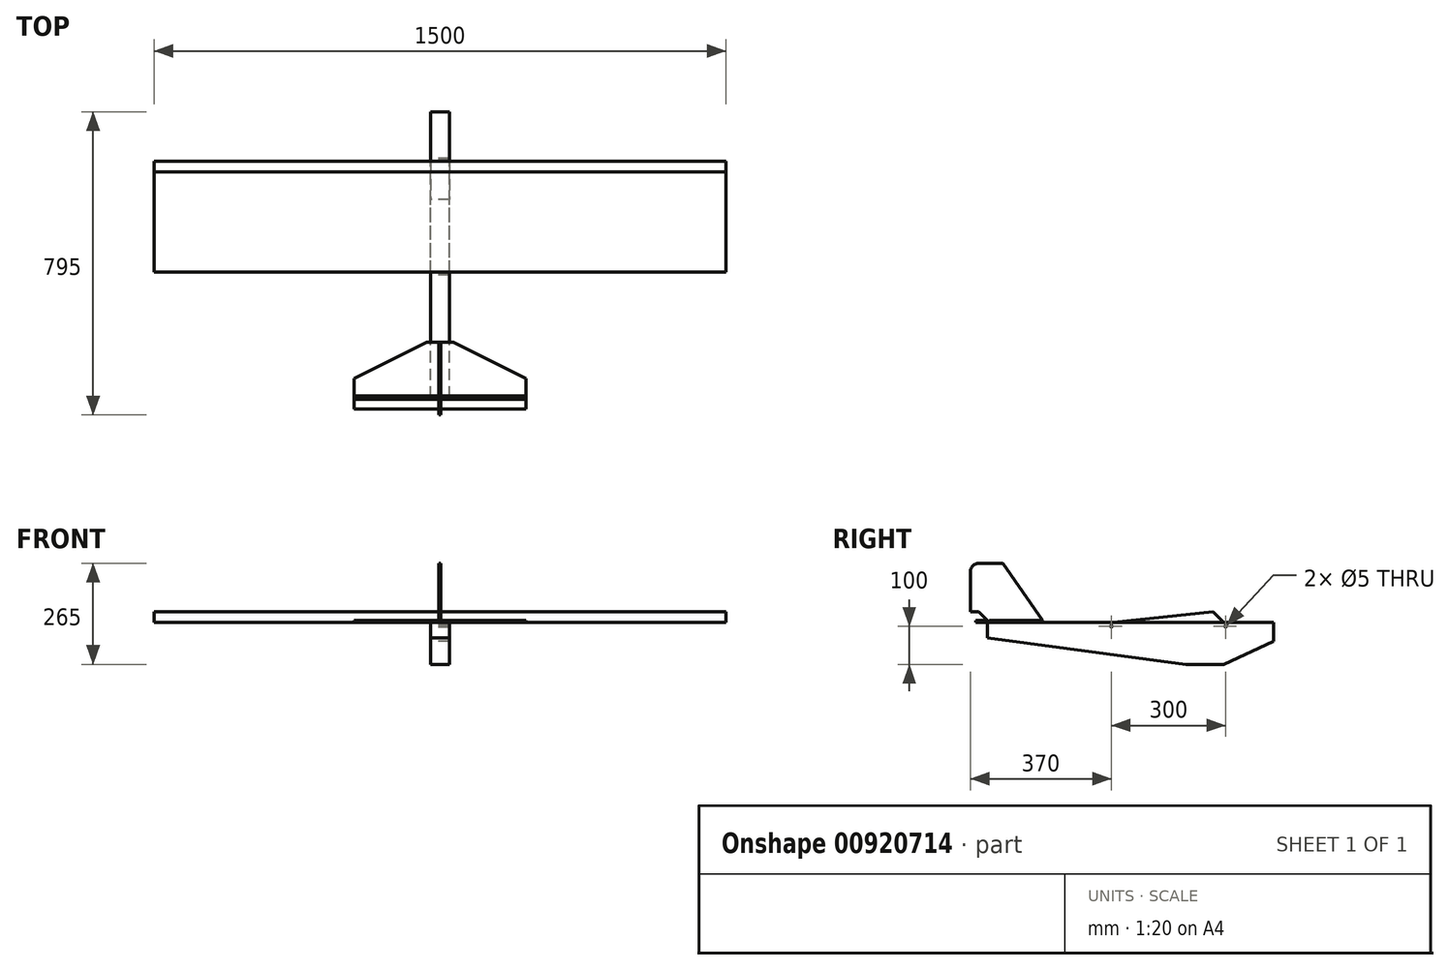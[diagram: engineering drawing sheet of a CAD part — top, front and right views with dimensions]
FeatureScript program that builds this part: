
annotation { "Feature Type Name" : "Feature", "Feature Type Description" : "" }
export const myFeature = defineFeature(function(context is Context, id is Id, definition is map)
    precondition{}
    {
        {
            var Q0;
            Q0=qCreatedBy(makeId("Right.planeOp"),FACE);
            var sketch = newSketch(context, id + "F0", { "sketchPlane" : qUnion([Q0])});
            skLineSegment(sketch, "E0.bottom", {"start": v(0, 0) * mm, "end": v(-750, 0) * mm});
            skLineSegment(sketch, "E0.left", {"start": v(0, 0) * mm, "end": v(0, 110) * mm});
            skLineSegment(sketch, "E0.right", {"start": v(-750, 0) * mm, "end": v(-750, 265) * mm});
            skLineSegment(sketch, "E1", {"start": v(-750, 110) * mm, "end": v(0, 110) * mm});
            skLineSegment(sketch, "E2", {"start": v(-605, 110) * mm, "end": v(-605, 115) * mm});
            skLineSegment(sketch, "E3", {"start": v(-605, 115) * mm, "end": v(-745, 115) * mm});
            skLineSegment(sketch, "E4", {"start": v(-750, 110) * mm, "end": v(-780, 110) * mm});
            skLineSegment(sketch, "E5", {"start": v(-780, 110) * mm, "end": v(-780, 115) * mm});
            skLineSegment(sketch, "E6", {"start": v(-780, 115) * mm, "end": v(-755, 115) * mm});
            skLineSegment(sketch, "E7", {"start": v(-420, 110) * mm, "end": v(-420, 25.58) * mm, "construction": true});
            skLineSegment(sketch, "E8", {"start": v(-130, 110) * mm, "end": v(-130, 0) * mm, "construction": true});
            skLineSegment(sketch, "E9", {"start": v(-750, 70) * mm, "end": v(-230, 0) * mm});
            skLineSegment(sketch, "E10", {"start": v(-230, 0) * mm, "end": v(-130, 0) * mm, "construction": true});
            skLineSegment(sketch, "E11", {"start": v(-130, 0) * mm, "end": v(0, 60) * mm});
            skLineSegment(sketch, "E12", {"start": v(-750, 110) * mm, "end": v(-755, 115) * mm});
            skLineSegment(sketch, "E13", {"start": v(-750, 110) * mm, "end": v(-745, 115) * mm});
            skPoint(sketch, "E14.orphan", {"position": v(-750, 115) * mm});
            skLineSegment(sketch, "E15", {"start": v(-750, 265) * mm, "end": v(-795, 265) * mm});
            skLineSegment(sketch, "E16", {"start": v(-795, 265) * mm, "end": v(-795, 137.5) * mm});
            skLineSegment(sketch, "E17", {"start": v(-772.5, 137.5) * mm, "end": v(-750, 115) * mm});
            skLineSegment(sketch, "E18", {"start": v(-772.5, 137.5) * mm, "end": v(-795, 137.5) * mm});
            skPoint(sketch, "E19.orphan", {"position": v(-795, 160) * mm});
            skLineSegment(sketch, "E20", {"start": v(-420, 110) * mm, "end": v(-157.58, 137.58) * mm});
            skLineSegment(sketch, "E21", {"start": v(-157.58, 137.58) * mm, "end": v(-130, 110) * mm});
            skCircle(sketch, "E22", {"center": v(-125, 100) * mm, "radius": 2.5 * mm});
            skCircle(sketch, "E23", {"center": v(-425, 100) * mm, "radius": 2.5 * mm});
            skLineSegment(sketch, "E24", {"start": v(-130, 7) * mm, "end": v(-180, 7) * mm});
            skLineSegment(sketch, "E25", {"start": v(-180, 7) * mm, "end": v(-180, 0) * mm});
            skLineSegment(sketch, "E26", {"start": v(-180, 3.5) * mm, "end": v(-130, 3.5) * mm, "construction": true});
            skLineSegment(sketch, "E27", {"start": v(-158.5, 7) * mm, "end": v(-158.5, 105) * mm, "construction": true});
            skLineSegment(sketch, "E28", {"start": v(-158.5, 105) * mm, "end": v(-151.5, 105) * mm, "construction": true});
            skLineSegment(sketch, "E29", {"start": v(-151.5, 105) * mm, "end": v(-151.5, 7) * mm, "construction": true});
            skPoint(sketch, "E30", {"position": v(-155, 3.5) * mm});
            skPoint(sketch, "E31", {"position": v(-155, 105) * mm});
            skLineSegment(sketch, "E32", {"start": v(-180, 7) * mm, "end": v(-158.5, 28.5) * mm, "construction": true});
            skLineSegment(sketch, "E33", {"start": v(-151.5, 28.5) * mm, "end": v(-130, 7) * mm, "construction": true});
            skLineSegment(sketch, "E34", {"start": v(-180, 105) * mm, "end": v(-130, 105) * mm, "construction": true});
            skLineSegment(sketch, "E35", {"start": v(-130, 105) * mm, "end": v(-151.5, 83.5) * mm, "construction": true});
            skLineSegment(sketch, "E36", {"start": v(-158.5, 83.5) * mm, "end": v(-180, 105) * mm, "construction": true});
            skArc(sketch, "E37", {"start": v(-772.5, 265) * mm, "mid": v(-788.4, 258.4) * mm, "end": v(-795, 242.5) * mm});
            skLineSegment(sketch, "E38", {"start": v(-750, 265) * mm, "end": v(-710.03, 265) * mm});
            skLineSegment(sketch, "E39", {"start": v(-710.03, 265) * mm, "end": v(-605, 115) * mm});
            skLineSegment(sketch, "E40", {"start": v(0, 60) * mm, "end": v(0, 110) * mm});
            skPoint(sketch, "E41", {"position": v(0, 85) * mm});
            skSolve(sketch);
        }
        {
            var Q0;
            {var subQ0=sQuery(id+"F0.wireOp",EDGE,"E17");Q0=makeQuery(id+"F0.imprint","IMPRINT",FACE,{"disambiguationData":[TD([[makeQuery(id+"F0.imprint","IMPRINT",EDGE,{"derivedFrom":subQ0}),1.0]])]});}
            var Q1;
            Q1=makeQuery(id+"F0.imprint","IMPRINT",FACE,{"disambiguationData":[TD([[makeQuery(id+"F0.imprint","IMPRINT",EDGE,{"derivedFrom":sQuery(id+"F0.wireOp",EDGE,"E3")}),-1.0]])]});
            extrude(context, id + "F1", {"entities" : qUnion([Q0, Q1]), "oppositeDirection" : true, "depth" : 5 * mm, "offsetDistance" : 25 * mm, "symmetric" : true});
        }
        {
            var Q0;
            {var subQ6=sQuery(id+"F0.wireOp",EDGE,"E9");Q0=makeQuery(id+"F0.imprint","IMPRINT",FACE,{"disambiguationData":[TD([[makeQuery(id+"F0.imprint","IMPRINT",EDGE,{"derivedFrom":subQ6}),1.0]])]});}
            extrude(context, id + "F2", {"entities" : qUnion([Q0]), "depth" : 50 * mm, "offsetDistance" : 25 * mm, "symmetric" : true});
        }
        {
            var Q0;
            Q0=makeQuery(id+"F0.imprint","IMPRINT",FACE,{"disambiguationData":[TD([[makeQuery(id+"F0.imprint","IMPRINT",EDGE,{"derivedFrom":sQuery(id+"F0.wireOp",EDGE,"E4")}),-1.0]])]});
            var Q1;
            {var subQ0=sQuery(id+"F0.wireOp",EDGE,"E2");Q1=makeQuery(id+"F0.imprint","IMPRINT",FACE,{"disambiguationData":[TD([[makeQuery(id+"F0.imprint","IMPRINT",EDGE,{"derivedFrom":subQ0}),1.0]])]});}
            extrude(context, id + "F3", {"entities" : qUnion([Q0, Q1]), "depth" : 450 * mm, "offsetDistance" : 25 * mm, "symmetric" : true});
        }
        {
            var Q0;
            Q0=makeQuery(id+"F3.opExtrude","SWEPT_FACE",FACE,{"disambiguationData":[OSD([sQuery(id+"F0.wireOp",EDGE,"E1")])]});
            var sketch = newSketch(context, id + "F4", { "sketchPlane" : qUnion([Q0])});
            skLineSegment(sketch, "E42.0.0", {"start": v(-225, 750) * mm, "end": v(-225, 605) * mm});
            skLineSegment(sketch, "E42.0.1", {"start": v(-225, 605) * mm, "end": v(225, 605) * mm});
            skLineSegment(sketch, "E42.0.2", {"start": v(225, 605) * mm, "end": v(225, 750) * mm});
            skLineSegment(sketch, "E42.0.3", {"start": v(225, 750) * mm, "end": v(-225, 750) * mm});
            skLineSegment(sketch, "E43", {"start": v(225, 700) * mm, "end": v(35, 605) * mm});
            skLineSegment(sketch, "E44", {"start": v(-35, 605) * mm, "end": v(-225, 700) * mm});
            skSolve(sketch);
        }
        {
            var Q0;
            {var subQ3=sQuery(id+"F4.wireOp",EDGE,"E43");Q0=makeQuery(id+"F4.imprint","IMPRINT",FACE,{"disambiguationData":[TD([[makeQuery(id+"F4.imprint","IMPRINT",EDGE,{"derivedFrom":subQ3}),1.0]])]});}
            var Q1;
            {var subQ3=sQuery(id+"F4.wireOp",EDGE,"E44");Q1=makeQuery(id+"F4.imprint","IMPRINT",FACE,{"disambiguationData":[TD([[makeQuery(id+"F4.imprint","IMPRINT",EDGE,{"derivedFrom":subQ3}),1.0]])]});}
            extrude(context, id + "F5", {"entities" : qUnion([Q0, Q1]), "operationType" : NewBodyOperationType.REMOVE, "oppositeDirection" : true, "depth" : 25 * mm, "offsetDistance" : 25 * mm});
        }
        {
            var Q0;
            {var subQ0=sQuery(id+"F0.wireOp",EDGE,"E20");Q0=makeQuery(id+"F0.imprint","IMPRINT",FACE,{"disambiguationData":[TD([[makeQuery(id+"F0.imprint","IMPRINT",EDGE,{"derivedFrom":subQ0}),-1.0]])]});}
            extrude(context, id + "F6", {"entities" : qUnion([Q0]), "operationType" : NewBodyOperationType.ADD, "depth" : 1500 * mm, "offsetDistance" : 25 * mm, "symmetric" : true});
        }
    });
